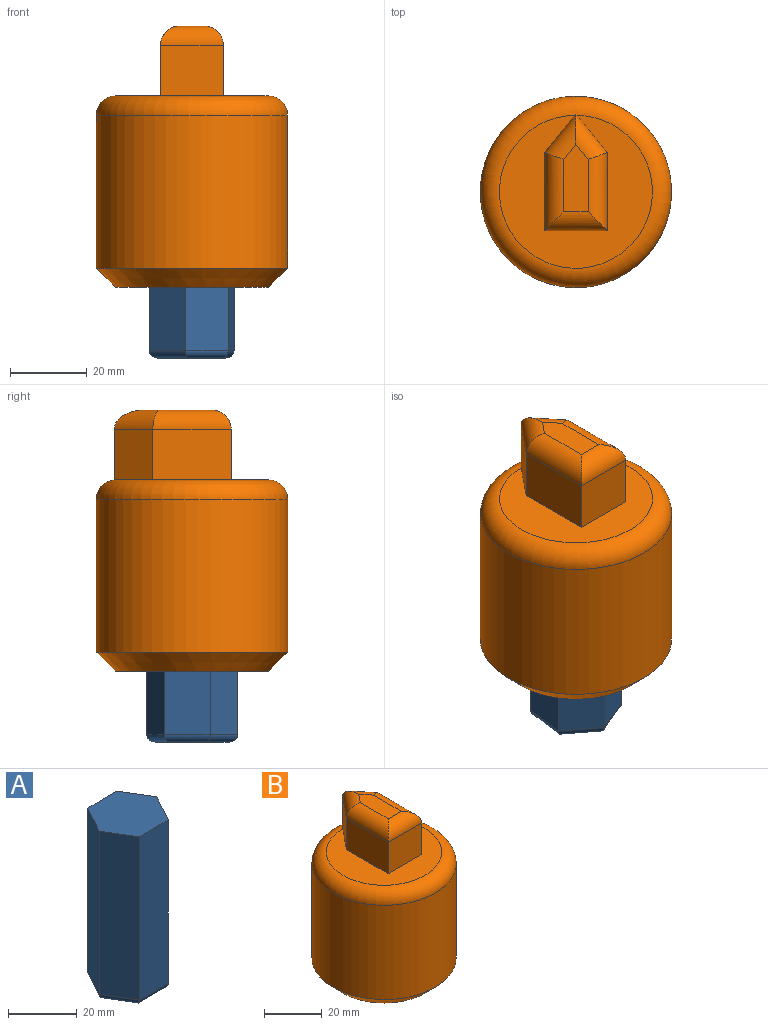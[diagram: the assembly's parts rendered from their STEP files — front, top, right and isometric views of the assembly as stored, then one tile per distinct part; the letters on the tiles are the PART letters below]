
ASSEMBLY  parts=2 mates=1
PART A: 14 faces, bbox 24x21x60 mm
  f0: plane 58x12.01mm, normal (0.01,-1,0), area 696.5mm2, adj f1,f5,f6,f10
  f1: plane 58x10.49mm, normal (0.87,-0.49,0), area 696.5mm2, adj f0,f2,f6,f8
  f2: plane 58x10.31mm, normal (0.86,0.51,0), area 696.5mm2, adj f1,f3,f6,f9
  f3: plane 58x12.01mm, normal (-0.01,1,0), area 696.5mm2, adj f2,f4,f6,f11
  f4: plane 58x10.49mm, normal (-0.87,0.49,0), area 696.5mm2, adj f3,f5,f6,f13
  f5: plane 58x10.31mm, normal (-0.86,-0.51,0), area 696.5mm2, adj f0,f4,f6,f12
  f6: plane 24.02x20.97mm, normal (0,0,1), area 374.7mm2, adj f0,f1,f2,f3,f4,f5
  f7: plane 19.4x16.94mm, normal (0,0,-1), area 244.4mm2, adj f8,f9,f10,f11,f12,f13
  f8: cylinder r=2mm len=11.46mm, axis (0.49,0.87,0), area 35.1mm2, adj f1,f7,f9,f10
  f9: cylinder r=2mm len=11.34mm, axis (-0.51,0.86,0), area 35.1mm2, adj f2,f7,f8,f11
  f10: cylinder r=2mm len=12.04mm, axis (1,0.01,0), area 35.1mm2, adj f0,f7,f8,f12
  f11: cylinder r=2mm len=12.04mm, axis (-1,-0.01,0), area 35.1mm2, adj f3,f7,f9,f13
  f12: cylinder r=2mm len=11.34mm, axis (0.51,-0.86,0), area 35.1mm2, adj f5,f7,f10,f13
  f13: cylinder r=2mm len=11.46mm, axis (-0.49,-0.87,0), area 35.1mm2, adj f4,f7,f11,f12
PART B: 23 faces, bbox 54.1x54.1x68.3 mm
  f0: plane 16.41x13.3mm, normal (0,-1,0), area 218.2mm2, adj f1,f4,f7,f9
  f1: plane 20.44x13.3mm, normal (1,0,0), area 271.9mm2, adj f0,f2,f7,f10
  f2: plane 13.31x10.09mm, normal (0.78,0.63,0), area 173mm2, adj f1,f3,f7,f12,f14
  f3: plane 13.31x10.09mm, normal (-0.78,0.63,0), area 173mm2, adj f2,f4,f7,f13,f14
  f4: plane 20.44x13.3mm, normal (-1,0,0), area 271.9mm2, adj f0,f3,f7,f11
  f5: plane 17.61x6.41mm, normal (0,0,1), area 100.2mm2, adj f9,f10,f11,f12,f13
  f6: cylinder r=25mm len=50mm, axis (0,0,-1), area 6283.2mm2, adj f14,f15
  f7: plane 40x40mm, normal (0,0,1), area 838.5mm2, adj f0,f1,f2,f3,f4,f14
  f8: plane 40x40mm, normal (0,0,-1), area 874.7mm2, adj f15,f16,f17,f18,f19,f20,f21
  f9: cylinder r=5mm len=16.41mm, axis (-1,0,0), area 100.3mm2, adj f0,f5,f10,f11
  f10: cylinder r=5mm len=20.44mm, axis (0,-1,0), area 141.2mm2, adj f1,f5,f9,f12
  f11: cylinder r=5mm len=20.44mm, axis (0,1,0), area 141.2mm2, adj f4,f5,f9,f13
  f12: cylinder r=5mm len=13.25mm, axis (0.63,-0.78,0), area 79.5mm2, adj f2,f5,f10,f13
  f13: cylinder r=5mm len=13.25mm, axis (0.63,0.78,0), area 79.5mm2, adj f3,f5,f11,f12
  f14: torus R=20mm, axis (0,0,1), area 1144mm2, adj f2,f3,f6,f7
  f15: cone r=25mm half-angle=45deg, axis (0,0,1), area 999.6mm2, adj f6,f8
  f16: plane 25x11.18mm, normal (0.39,-0.92,0), area 303.1mm2, adj f8,f17,f21,f22
  f17: plane 25x9.65mm, normal (-0.61,-0.8,0), area 303.1mm2, adj f8,f16,f18,f22
  f18: plane 25x12.03mm, normal (-0.99,0.13,0), area 303.1mm2, adj f8,f17,f19,f22
  f19: plane 25x11.18mm, normal (-0.39,0.92,0), area 303.1mm2, adj f8,f18,f20,f22
  f20: plane 25x9.65mm, normal (0.61,0.8,0), area 303.1mm2, adj f8,f19,f21,f22
  f21: plane 25x12.03mm, normal (0.99,-0.13,0), area 303.1mm2, adj f8,f16,f20,f22
  f22: plane 24.05x22.37mm, normal (0,0,-1), area 381.9mm2, adj f16,f17,f18,f19,f20,f21
PLACE A rot(axis=(0,0,1),21.9deg) t=(-28.56,-5.98,-36.81)mm
PLACE B t=(-28.5,-5.9,6.69)mm
MATE parallel A.f5 <-> B.f20  axis (-0.61,-0.8,0) through (-34.86,-14.25,-5.81)mm
